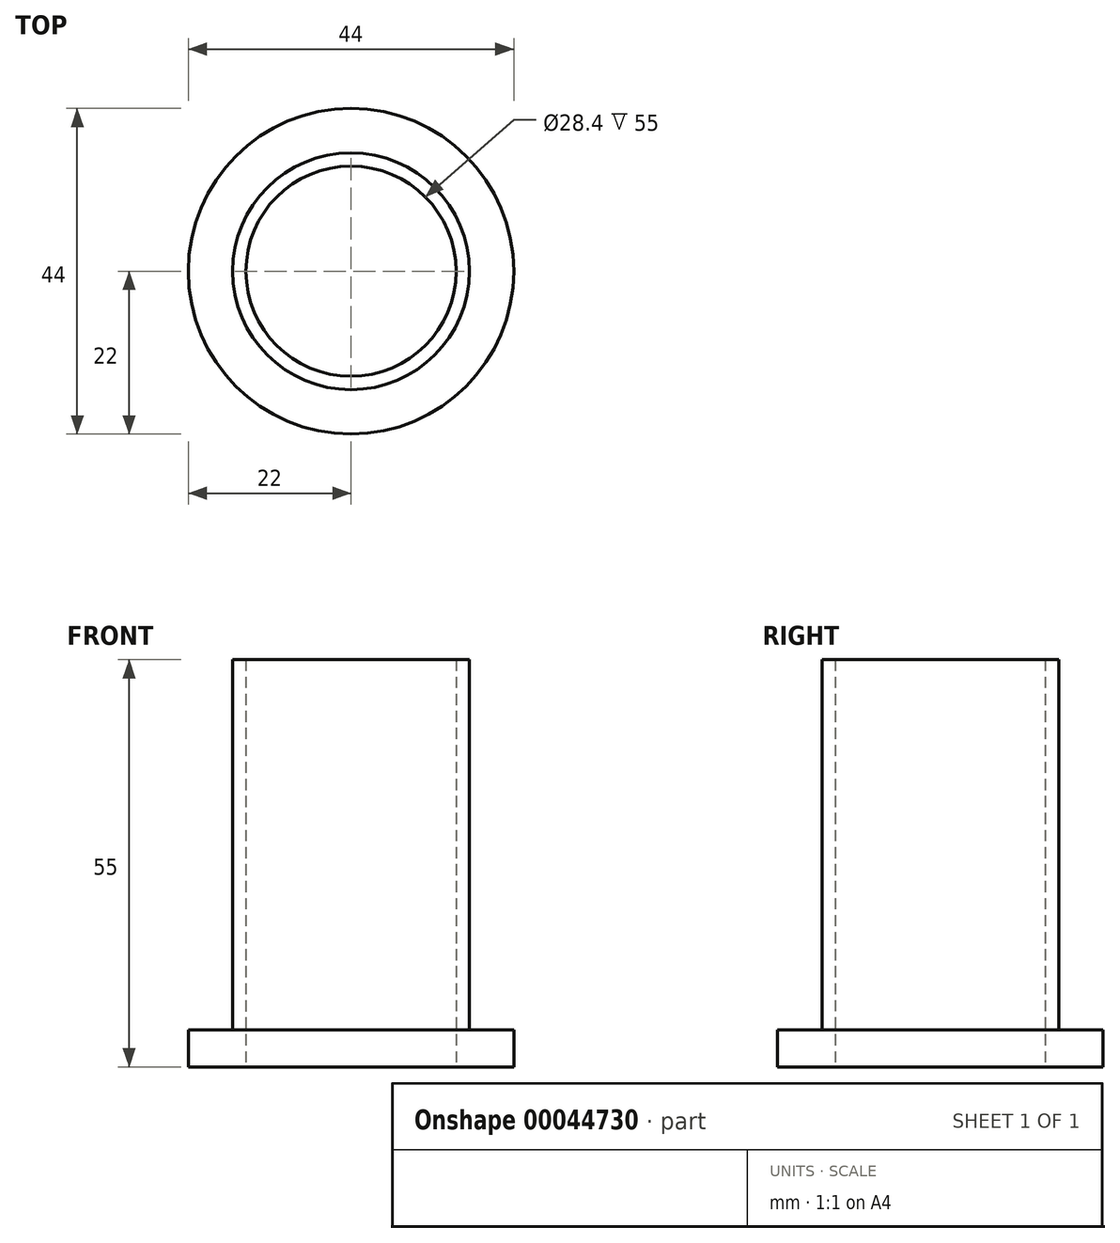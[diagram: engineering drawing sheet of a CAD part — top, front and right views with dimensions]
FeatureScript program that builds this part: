
annotation { "Feature Type Name" : "Feature", "Feature Type Description" : "" }
export const myFeature = defineFeature(function(context is Context, id is Id, definition is map)
    precondition{}
    {
        {
            var Q0;
            Q0=qCreatedBy(makeId("Top.planeOp"),FACE);
            var sketch = newSketch(context, id + "F0", { "sketchPlane" : qUnion([Q0])});
            skCircle(sketch, "E0", {"center": v(0, 0) * mm, "radius": 16 * mm});
            skSolve(sketch);
        }
        {
            var Q0;
            Q0 = qSketchRegion(id + "F0", true);
            extrude(context, id + "F1", {"entities" : qUnion([Q0]), "depth" : 55 * mm});
        }
        {
            var Q0;
            Q0=qCreatedBy(makeId("Top.planeOp"),FACE);
            var sketch = newSketch(context, id + "F2", { "sketchPlane" : qUnion([Q0])});
            skCircle(sketch, "E1", {"center": v(0, 0) * mm, "radius": 22 * mm});
            skSolve(sketch);
        }
        {
            var Q0;
            Q0 = qSketchRegion(id + "F2", true);
            extrude(context, id + "F3", {"entities" : qUnion([Q0]), "operationType" : NewBodyOperationType.ADD, "flatOperationType" : FlatOperationType.REMOVE, "offsetDistance" : 25 * mm, "depth" : 5 * mm, "domain" : OperationDomain.MODEL});
        }
        {
            var Q0;
            Q0=makeQuery(id+"F3.boolean.opBoolean","MERGE",FACE,{"derivedFrom":[makeQuery(id+"F1.opExtrude","CAP_FACE",FACE,{"disambiguationData":[OSD([sQuery(id+"F0.wireOp",EDGE,"E0")])],"isStart":true}),makeQuery(id+"F3.opExtrude","CAP_FACE",FACE,{"disambiguationData":[OSD([sQuery(id+"F2.wireOp",EDGE,"E1")])],"isStart":true})]});
            var sketch = newSketch(context, id + "F4", { "sketchPlane" : qUnion([Q0])});
            skPoint(sketch, "E2", {"position": v(0, 0) * mm});
            skSolve(sketch);
        }
        {
            var Q0;
            Q0=sQuery(id+"F4.wireOp",VERTEX,"E2");
            var Q1;
            Q1=makeQuery(id+"F1.opExtrude","SWEPT_BODY",BODY,{"disambiguationData":[OSD([sQuery(id+"F0.wireOp",EDGE,"E0")])]});
            hole(context, id + "F5", {"style" : HoleStyle.SIMPLE, "holeDiameter" : 28.4 * mm, "endStyle" : HoleEndStyle.THROUGH, "locations" : qUnion([Q0]), "scope" : qUnion([Q1]), "isTappedThrough" : true});
        }
    });
